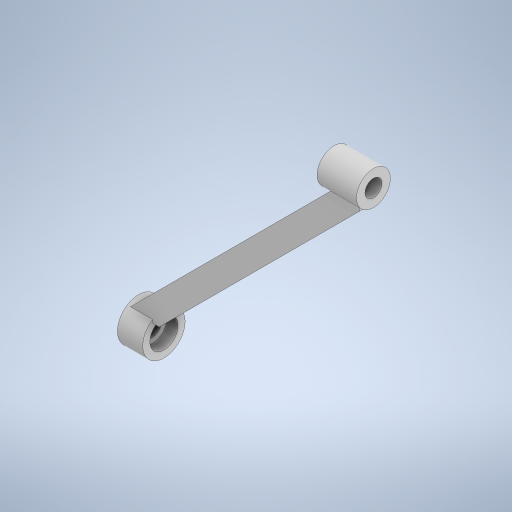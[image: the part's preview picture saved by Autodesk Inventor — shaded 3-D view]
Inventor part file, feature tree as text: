
AUTODESK INVENTOR PART (.ipt)
format: ipt  version: 2023 (Build 270158000, 158)  size: 295,424 bytes
history: native  units: mm
features: extrude x5, sketch x4, projected_geometry x2, plane x1
ambient origin geometry x8: Origin, YZ Plane, XZ Plane, XY Plane, X Axis, Y Axis, Z Axis, Center Point
bodies: Solid1 (feature_tree)
feature tree (12):
  sketch  "Sketch1"  dims[d0=6.0mm d1=12.0mm]
  extrude  "Extrusion1"  Depth=12.0mm
  extrude  "Extrusion2"  Depth=14.0mm
  extrude  "Extrusion3"  Depth=4.0mm
  plane  "Work Plane1"
  extrude  "Extrusion4"  Depth=8.0mm TaperAngle=0.0deg
  extrude  "Extrusion5"  Depth=4.0mm
  sketch  "Sketch2"  dims[d2=14.0mm d3=0.0mm d4=100.0mm]
  projected_geometry  "Projected Loop1"
  sketch  "Sketch3"  dims[d5=45.0deg d6=4.0mm]
  projected_geometry  "Projected Loop2"
  sketch  "Sketch4"  dims[d7=4.0mm d8=8.0mm d9=0.0mm d10=8.871019mm d12=60.0mm d13=2.0mm d14=0.0mm d15=15.0mm d16=6.0mm d17=5.240974mm d18=9.0mm d19=0.0mm d20=10.0mm d21=9.0mm d22=4.0mm d23=0.0mm d24=0.0mm]
